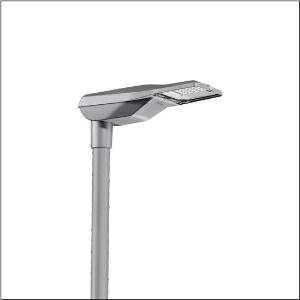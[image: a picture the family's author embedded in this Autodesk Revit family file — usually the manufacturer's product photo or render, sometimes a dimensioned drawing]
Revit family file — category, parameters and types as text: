
# Revit family: streetlight_sl_21_iq_micro___st0_8a_5xe1c31d08db_b6ee
name_source: partatom
category: Lighting Fixtures
units: mm (PartAtom-declared; Revit-internal decimal feet)

## family parameters
Cut with Voids When Loaded = No
Host = Face
Light Source = No
Part Type = Normal
Room Calculation Point = No
Round Connector Dimension = Use Diameter
Shared = No

## types (1)
- --- (1 x LED, 4810 lm, 36.4 W, 3000K)
    Apparent Load = 36 VA
    CIE Flux Codes = 38 75 97 100 100
    Color Rendering = 70
    Color Temperature = 3000K
    Default Elevation = 1800 mm
    Description = Streetlight SL 21 iQ micro, mast luminaire, primary light control with lens, of PMMA, primary optical cover: cover, of toughened safety glass, transparent, light distribution: ST0.8a, light emission: direct distribution, primary light characteristic: asymmetric, installation type: post-top, side-entry, LED, High Power LED, rated luminous flux: 4.810lm, luminous efficacy: 132lm/W, light colour: 730, colour temperature: 3000K, control: Auto-Match, Temp-Guard, Lumen-Switch, Night-Set, Smart-Wire, Light-Fading, Desk-Remote (wireless, voltage-free reading and setting of iQ features in the workshop via application-optimized NFC function/RFID function), optimised constant luminous flux control (CLO 2.0), presetting dimming linear, mains connection: 220..240V, AC, 50/60Hz, start of lifetime: 36W, end of service life: 38W, reduction: 16W, luminaire housing, of diecast aluminium, powder-coated, Siteco® metallic grey (DB 702S), corrosivity category C5 mid according to DIN EN ISO 12944, please order mast flange separately, inclination adjustable: 0°, 5°, 10°, 15°, sealing non-destructively replaceable, multi-level sealing system, length: 528mm, width: 235mm, height: 110mm, mast flange for spigot size: 42mm (side-entry): 5XC10008XM4, 60/48mm (side-entry/post-top): 5XC10108XM2, 76/60mm (side-entry/post-top): 5XC10108XM1, protection rating (complete): IP66, insulation class (complete): insulation class II (safety insulation), certification: CE, ENEC, ENEC+, VDE, impact resistance: IK09, permissible operating ambient temperature for outdoor applications: -40..+50°C, standard-compliant lighting for roads and squares, packaging unit: 1 piece

Light Distribution: ST0.8a
    Height = 110 mm
    Lamp = 1 x LED
    Lamp Light Flux = 4810 lm
    Lamp Power = 36.4 W
    Lamp count = 1
    Length = 528 mm
    Luminous efficacy = 132 lm/W
    Manufacturer = Siteco
    ModVariant = No
    Model = 5XE1C31D08DB
    Number of Poles = 1
    OnlyDefault = Yes
    Power Factor = 1
    Product Name = Streetlight SL 21 iQ micro | ST0.8a
    Product group = mast luminaire | pylon top
    ProductGroupID = 6100
    Protection Class = Protection class II
    Protection Degree = IP 66
    RLX_Detail_Level = 1
    RLX_Emergency_Light_Flux = 0 lm
    RLX_Emergency_Type = 0
    RLX_Emergency_Type_DB = No
    RlxData = <blob elided: 98897 chars, md5=cee21a0a>
    Socket = socket
    Standby Power = 0 W
    System Light Flux = 4810 lm
    System Power = 36 W
    Type Comments = factory setting: luminous flux: 100 % | dim-lin: 254 | 715 mA
    Type Image = l_1006881.jpg
    URL = http://relux.com
    VarID = @adj_086883
    Voltage = 0 V
    Weight = 0.00 kg
    Width = 235 mm

## geometry (parser evidence)
native form markers: Blend x4, Sweep x9
no freeform markers — native parametric forms only
